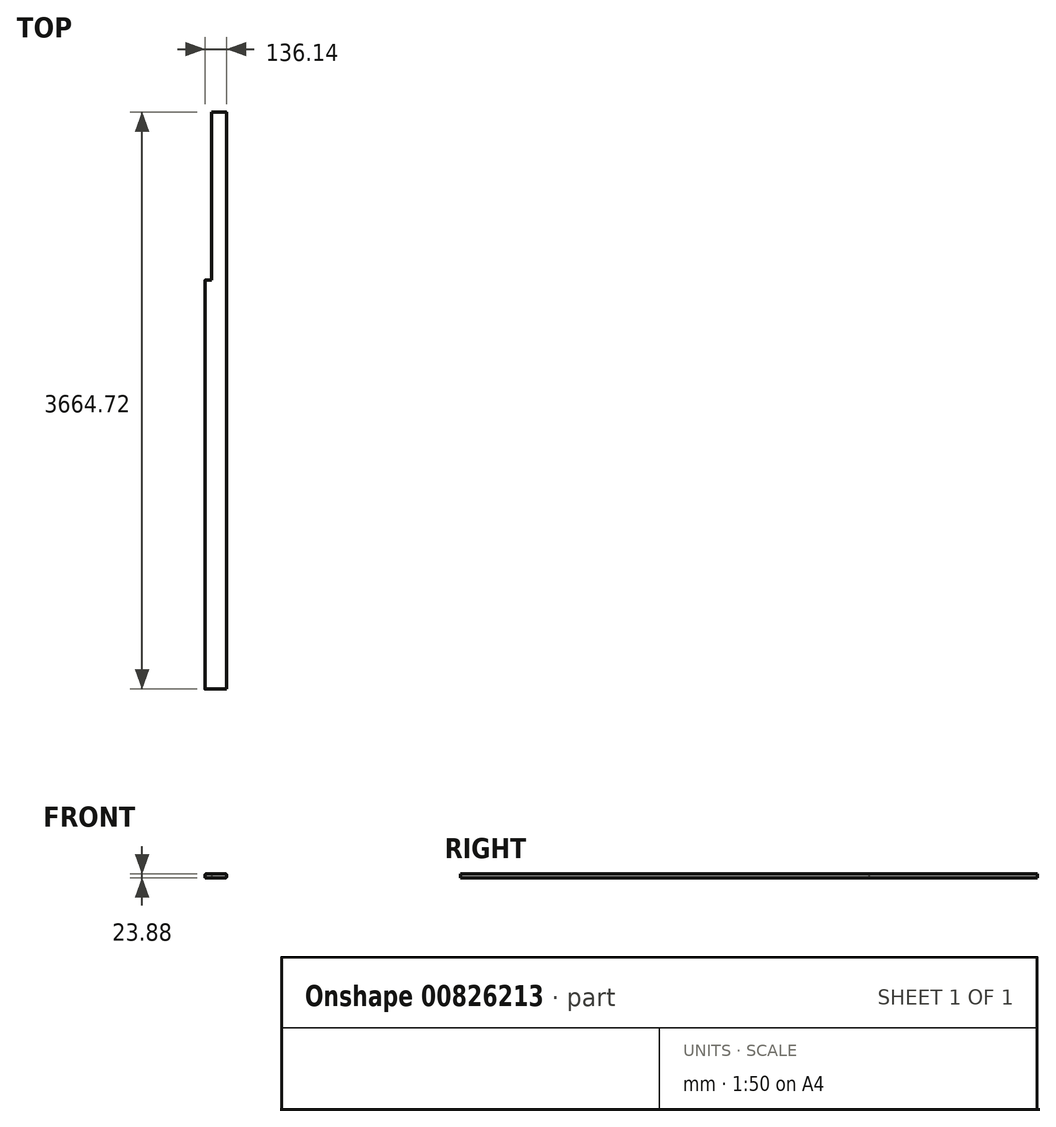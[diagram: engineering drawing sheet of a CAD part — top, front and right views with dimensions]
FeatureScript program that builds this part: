
annotation { "Feature Type Name" : "Feature", "Feature Type Description" : "" }
export const myFeature = defineFeature(function(context is Context, id is Id, definition is map)
    precondition{}
    {
        {
            var Q0;
            Q0=qCreatedBy(makeId("Front.planeOp"),FACE);
            var sketch = newSketch(context, id + "F0", { "sketchPlane" : qUnion([Q0])});
            skLineSegment(sketch, "E0.bottom", {"start": v(-63.25, 11.94) * mm, "end": v(63.25, 11.94) * mm});
            skLineSegment(sketch, "E0.top", {"start": v(-63.25, -11.94) * mm, "end": v(63.25, -11.94) * mm});
            skLineSegment(sketch, "E0.left", {"start": v(-68.07, 7.11) * mm, "end": v(-68.07, -7.11) * mm});
            skLineSegment(sketch, "E0.right", {"start": v(68.07, 7.11) * mm, "end": v(68.07, -7.11) * mm});
            skPoint(sketch, "E0.middle", {"position": v(0, 0) * mm});
            skPoint(sketch, "E1.visualSharp", {"position": v(-68.07, 11.94) * mm});
            skArc(sketch, "E1.filletArc", {"start": v(-63.25, 11.94) * mm, "mid": v(-66.66, 10.52) * mm, "end": v(-68.07, 7.11) * mm});
            skPoint(sketch, "E2.visualSharp", {"position": v(68.07, 11.94) * mm});
            skArc(sketch, "E2.filletArc", {"start": v(68.07, 7.11) * mm, "mid": v(66.66, 10.52) * mm, "end": v(63.25, 11.94) * mm});
            skPoint(sketch, "E3.visualSharp", {"position": v(68.07, -11.94) * mm});
            skArc(sketch, "E3.filletArc", {"start": v(63.25, -11.94) * mm, "mid": v(66.66, -10.52) * mm, "end": v(68.07, -7.11) * mm});
            skPoint(sketch, "E4.visualSharp", {"position": v(-68.07, -11.94) * mm});
            skArc(sketch, "E4.filletArc", {"start": v(-68.07, -7.11) * mm, "mid": v(-66.66, -10.52) * mm, "end": v(-63.25, -11.94) * mm});
            skSolve(sketch);
        }
        {
            var Q0;
            Q0=makeQuery(id+"F0.imprint","IMPRINT",FACE,{"disambiguationData":[TD([[makeQuery(id+"F0.imprint","IMPRINT",EDGE,{"derivedFrom":sQuery(id+"F0.wireOp",EDGE,"E0.bottom")}),-1.0]])]});
            extrude(context, id + "F1", {"entities" : qUnion([Q0]), "endBound" : BoundingType.SYMMETRIC, "depth" : 3664.71 * mm, "offsetDistance" : 25.4 * mm});
        }
        {
            var Q0;
            Q0=makeQuery(id+"F1.opExtrude","SWEPT_FACE",FACE,{"disambiguationData":[OSD([sQuery(id+"F0.wireOp",EDGE,"E0.bottom")])]});
            var sketch = newSketch(context, id + "F2", { "sketchPlane" : qUnion([Q0])});
            skLineSegment(sketch, "E5.bottom", {"start": v(-27.64, 1893.5) * mm, "end": v(-289.09, 1893.5) * mm});
            skLineSegment(sketch, "E5.top", {"start": v(-27.64, 765.56) * mm, "end": v(-289.09, 765.56) * mm});
            skLineSegment(sketch, "E5.left", {"start": v(-27.64, 1893.5) * mm, "end": v(-27.64, 765.56) * mm});
            skLineSegment(sketch, "E5.right", {"start": v(-289.09, 1893.5) * mm, "end": v(-289.09, 765.56) * mm});
            skSolve(sketch);
        }
        {
            var Q0;
            Q0 = qSketchRegion(id + "F2", true);
            extrude(context, id + "F3", {"entities" : qUnion([Q0]), "operationType" : NewBodyOperationType.REMOVE, "endBound" : BoundingType.THROUGH_ALL, "oppositeDirection" : true, "depth" : 25.4 * mm, "offsetDistance" : 25.4 * mm});
        }
    });
